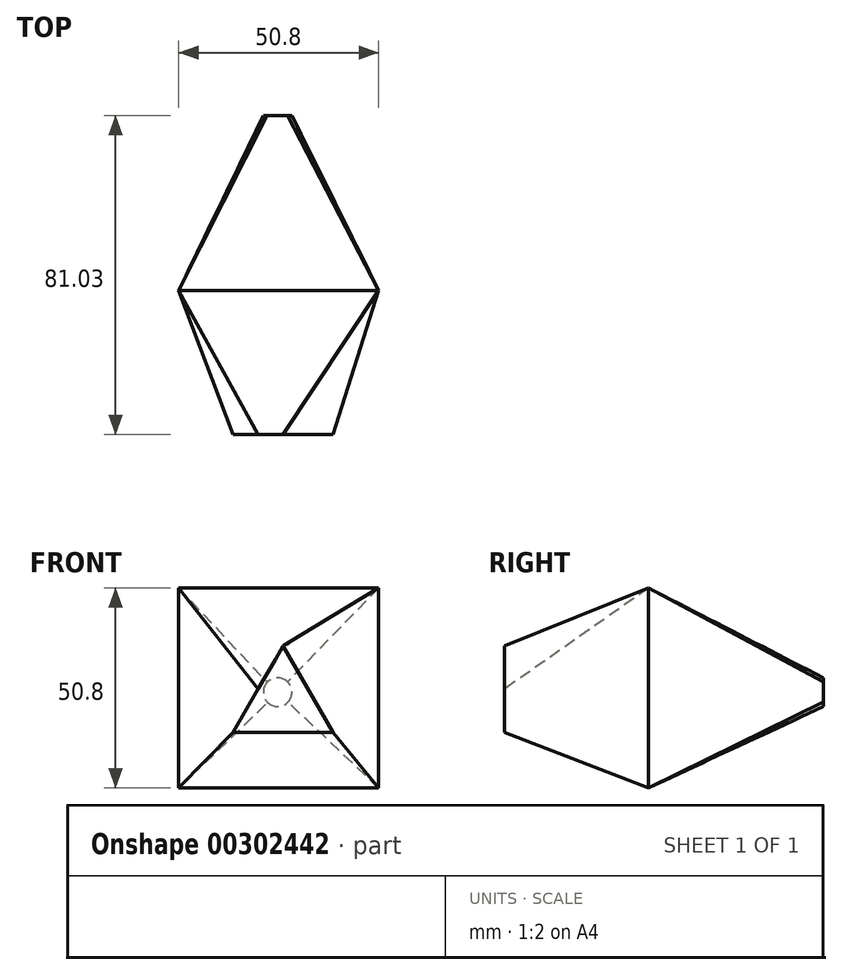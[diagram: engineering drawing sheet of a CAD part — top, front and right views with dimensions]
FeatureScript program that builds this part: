
annotation { "Feature Type Name" : "Feature", "Feature Type Description" : "" }
export const myFeature = defineFeature(function(context is Context, id is Id, definition is map)
    precondition{}
    {
        {
            var Q0;
            Q0=qCreatedBy(makeId("Front.planeOp"),FACE);
            var sketch = newSketch(context, id + "F0", { "sketchPlane" : qUnion([Q0])});
            skLineSegment(sketch, "E0", {"start": v(0, 0) * mm, "end": v(-50.8, 0) * mm});
            skLineSegment(sketch, "E1", {"start": v(-51.25, 0.23) * mm, "end": v(-51.25, 51.03) * mm});
            skLineSegment(sketch, "E2", {"start": v(-50.8, 50.8) * mm, "end": v(0, 50.8) * mm});
            skLineSegment(sketch, "E3", {"start": v(0, 50.8) * mm, "end": v(0, 0) * mm});
            skLineSegment(sketch, "E4.top", {"start": v(-50.8, 0) * mm, "end": v(0, 0) * mm});
            skLineSegment(sketch, "E4.left", {"start": v(-50.8, 50.8) * mm, "end": v(-50.8, 0) * mm});
            skSolve(sketch);
        }
        {
            var Q0;
            Q0=qCreatedBy(makeId("Front.planeOp"),FACE);
            cPlane(context, id + "F1", {"entities" : qUnion([Q0]), "cplaneType" : CPlaneType.OFFSET, "offset" : 36.58 * mm, "width" : 152.4 * mm, "height" : 152.4 * mm});
        }
        {
            var Q0;
            Q0=qCreatedBy(id+"F1.planeOp",FACE);
            var sketch = newSketch(context, id + "F2", { "sketchPlane" : qUnion([Q0])});
            skLineSegment(sketch, "E5", {"start": v(-36.97, 14.1) * mm, "end": v(-11.57, 14.1) * mm});
            skLineSegment(sketch, "E6", {"start": v(-11.57, 14.1) * mm, "end": v(-24.27, 36.1) * mm});
            skLineSegment(sketch, "E7", {"start": v(-24.27, 36.1) * mm, "end": v(-36.97, 14.1) * mm});
            skSolve(sketch);
        }
        {
            var Q0;
            Q0=makeQuery(id+"F0.imprint","IMPRINT",FACE,{"disambiguationData":[TD([[makeQuery(id+"F0.imprint","IMPRINT",EDGE,{"derivedFrom":sQuery(id+"F0.wireOp",EDGE,"E2")}),-1.0]])]});
            var Q1;
            Q1=makeQuery(id+"F2.imprint","IMPRINT",FACE,{"disambiguationData":[TD([[makeQuery(id+"F2.imprint","IMPRINT",EDGE,{"derivedFrom":sQuery(id+"F2.wireOp",EDGE,"E5")}),1.0]])]});
            loft(context, id + "F3", {"sheetProfilesArray" : [{ "sheetProfileEntities" : qUnion([Q0]) }, { "sheetProfileEntities" : qUnion([Q1]) }]});
        }
        {
            var Q0;
            Q0=qCreatedBy(makeId("Front.planeOp"),FACE);
            cPlane(context, id + "F4", {"entities" : qUnion([Q0]), "cplaneType" : CPlaneType.OFFSET, "offset" : 44.45 * mm, "oppositeDirection" : true, "width" : 152.4 * mm, "height" : 152.4 * mm});
        }
        {
            var Q0;
            Q0=qCreatedBy(id+"F4.planeOp",FACE);
            var sketch = newSketch(context, id + "F5", { "sketchPlane" : qUnion([Q0])});
            skCircle(sketch, "E8", {"center": v(-25.67, 24.31) * mm, "radius": 3.64 * mm});
            skSolve(sketch);
        }
        {
            var Q1;
            Q1=makeQuery(id+"F3.opLoft","CAP_FACE",FACE,{"disambiguationData":[OSD([makeQuery(id+"F0.imprint","IMPRINT",FACE,{"disambiguationData":[TD([[makeQuery(id+"F0.imprint","IMPRINT",EDGE,{"derivedFrom":sQuery(id+"F0.wireOp",EDGE,"E2")}),-1.0]])]})])],"isStart":true});
            var Q2;
            Q2=makeQuery(id+"F5.imprint","IMPRINT",FACE,{"disambiguationData":[TD([[makeQuery(id+"F5.imprint","IMPRINT",EDGE,{"derivedFrom":sQuery(id+"F5.wireOp",EDGE,"E8")}),1.0]])]});
            loft(context, id + "F6", {"operationType" : NewBodyOperationType.ADD, "sheetProfilesArray" : [{ "sheetProfileEntities" : qUnion([Q1]) }, { "sheetProfileEntities" : qUnion([Q2]) }]});
        }
    });
